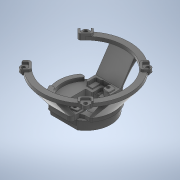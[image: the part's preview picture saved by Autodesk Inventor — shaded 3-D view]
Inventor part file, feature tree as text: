
AUTODESK INVENTOR PART (.ipt)
format: ipt  version: 2020 (Build 240168000, 168)  size: 1,462,784 bytes
history: native  units: mm
features: projected_geometry x52, sketch x31, extrude x24, other x9, fillet x9, chamfer x4, loft x2, revolve x1, pattern_circular x1, mirror x1
ambient origin geometry x8: Origin, YZ Plane, XZ Plane, XY Plane, X Axis, Y Axis, Z Axis, Center Point
bodies: Body1 (feature_tree)
feature tree (134):
  other  "Твердое тело1"
  extrude  "Выдавливание1"  Depth=17.1mm
  extrude  "Выдавливание2"  Depth=17.1mm
  other  "РабПлоскость1"
  sketch  "Эскиз3"
  other  "РабОсь1"
  revolve  "Вращение1"
  extrude  "Выдавливание3"  Depth=25.0mm
  extrude  "Выдавливание4"  Depth=5.3mm
  extrude  "Выдавливание5"  Depth=44.7mm
  extrude  "Выдавливание6"  Depth=7.7mm TaperAngle=0.0deg
  extrude  "Выдавливание7"  Depth=5.0mm
  extrude  "Выдавливание8"  Depth=30.65mm
  sketch  "Эскиз10"
  extrude  "Выдавливание9"  Depth=2.5mm TaperAngle=0.0deg
  fillet  "Сопряжение1"  Radius=0.2mm
  fillet  "Сопряжение2"  [1 undecoded]
  fillet  "Сопряжение3"  Radius=1.85mm
  extrude  "Выдавливание10"  Depth=30.0mm
  fillet  "Сопряжение4"  Radius=2.0mm
  fillet  "Сопряжение5"  Radius=3.0mm
  extrude  "камера"  Depth=38.0mm
  extrude  "труба"  Depth=10.0mm TaperAngle=0.0deg
  sketch  "Эскиз15"
  other  "РабПлоскость2"
  extrude  "Выдавливание12"  Depth=5.2mm
  extrude  "Выдавливание13"  Depth=6.2mm
  chamfer  "Фаска1"  Distance=29.46mm
  fillet  "Сопряжение6"  Radius=10.0mm
  fillet  "Сопряжение7"  Radius=9.5mm
  other  "РабОсь2"
  pattern_circular  "Круговой массив1"  [2 undecoded]
  extrude  "Выдавливание15"  TaperAngle=60.0deg  [1 undecoded]
  chamfer  "Фаска2"  Distance=6.0mm
  sketch  "Эскиз20"
  extrude  "Выдавливание16"  Depth=6.0mm
  fillet  "Сопряжение8"  Radius=14.2mm
  other  "РабПлоскость3"
  extrude  "Выдавливание17"  Depth=9.5mm
  extrude  "Выдавливание18"  Depth=2.0mm
  sketch  "Эскиз24"
  sketch  "Эскиз25"
  sketch  "Эскиз26"
  extrude  "Выдавливание19"  Depth=13.962634mm
  loft  "Лофт1"
  other  "РабПлоскость4"
  mirror  "Зеркальное отражение1"
  extrude  "Выдавливание20"  Depth=2.0mm TaperAngle=0.0deg
  loft  "Лофт2"
  extrude  "Выдавливание21"  Depth=6.2mm
  chamfer  "Фаска3"  Distance=6.0mm
  chamfer  "Фаска4"  Distance=1.7mm
  extrude  "Выдавливание22"  Depth=1.5mm TaperAngle=0.0deg
  extrude  "Выдавливание23"  Depth=6.0mm TaperAngle=0.0deg
  fillet  "Сопряжение9"  Radius=0.5mm
  extrude  "Выдавливание24"  Depth=0.7mm
  sketch  "Эскиз1"
  sketch  "Эскиз2"
  projected_geometry  "Спроецированная петля1"
  projected_geometry  "Спроецированная петля2"
  sketch  "Эскиз4"
  projected_geometry  "Спроецированная петля3"
  sketch  "Эскиз5"
  sketch  "Эскиз6"
  projected_geometry  "Спроецированная петля4"
  sketch  "Эскиз7"
  projected_geometry  "Спроецированная петля5"
  sketch  "Эскиз8"
  projected_geometry  "Спроецированная петля6"
  projected_geometry  "Спроецированная петля7"
  projected_geometry  "Спроецированная петля8"
  sketch  "Эскиз9"
  projected_geometry  "Спроецированная петля9"
  projected_geometry  "Спроецированная петля10"
  projected_geometry  "Спроецированная петля11"
  projected_geometry  "Спроецированная петля12"
  sketch  "Эскиз11"
  sketch  "Эскиз12"
  projected_geometry  "Спроецированная петля13"
  projected_geometry  "Спроецированная петля14"
  projected_geometry  "Спроецированная петля15"
  sketch  "Эскиз14"
  projected_geometry  "Спроецированная петля20"
  projected_geometry  "Спроецированная петля21"
  projected_geometry  "Спроецированная петля22"
  projected_geometry  "Спроецированная петля23"
  sketch  "Эскиз16"
  projected_geometry  "Спроецированная петля24"
  sketch  "Эскиз17"
  projected_geometry  "Спроецированная петля25"
  sketch  "Эскиз18"
  sketch  "Эскиз19"
  projected_geometry  "Спроецированная петля26"
  projected_geometry  "Спроецированная петля27"
  projected_geometry  "Спроецированная петля28"
  projected_geometry  "Спроецированная петля29"
  sketch  "Эскиз21"
  projected_geometry  "Спроецированная петля30"
  projected_geometry  "Спроецированная петля31"
  projected_geometry  "Спроецированная петля32"
  projected_geometry  "Спроецированная петля33"
  projected_geometry  "Спроецированная петля34"
  projected_geometry  "Спроецированная петля35"
  projected_geometry  "Спроецированная петля36"
  projected_geometry  "Спроецированная петля37"
  projected_geometry  "Спроецированная петля38"
  projected_geometry  "Спроецированная петля39"
  sketch  "Эскиз22"
  projected_geometry  "Спроецированная петля40"
  projected_geometry  "Спроецированная петля41"
  projected_geometry  "Спроецированная петля42"
  projected_geometry  "Спроецированная петля43"
  projected_geometry  "Спроецированная петля44"
  sketch  "Эскиз23"
  projected_geometry  "Спроецированная петля45"
  projected_geometry  "Спроецированная петля46"
  projected_geometry  "Спроецированная петля47"
  projected_geometry  "Спроецированная петля48"
  projected_geometry  "Спроецированная петля49"
  projected_geometry  "Спроецированная петля50"
  other  "Ребра1"
  sketch  "Эскиз27"
  projected_geometry  "Спроецированная петля51"
  sketch  "Эскиз28"
  projected_geometry  "Спроецированная петля52"
  projected_geometry  "Спроецированная петля53"
  other  "Ребра2"
  sketch  "Эскиз31"
  sketch  "Эскиз32"
  projected_geometry  "Спроецированная петля54"
  projected_geometry  "Спроецированная петля55"
  sketch  "Эскиз33"
  projected_geometry  "Спроецированная петля56"
  sketch  "Эскиз34"
note: 4 required parameter values undecoded (feature->parameter linkage not recoverable at this tier; creation-order binding heuristic only, values carry confidence <= 0.55)
